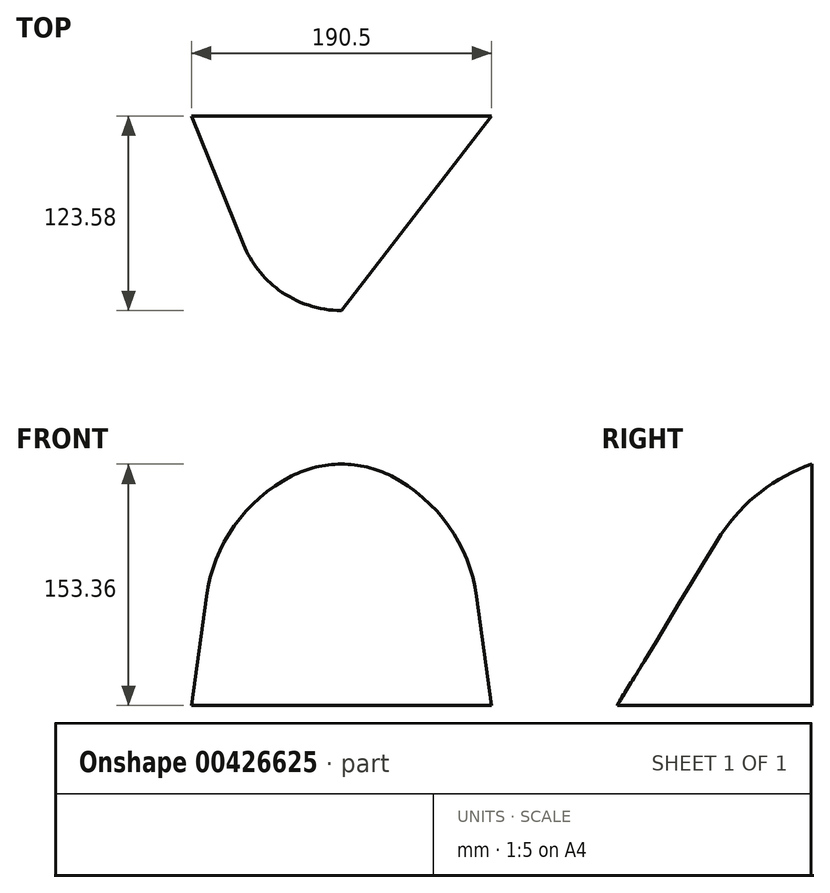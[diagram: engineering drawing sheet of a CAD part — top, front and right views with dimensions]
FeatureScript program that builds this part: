
annotation { "Feature Type Name" : "Feature", "Feature Type Description" : "" }
export const myFeature = defineFeature(function(context is Context, id is Id, definition is map)
    precondition{}
    {
        {
            var Q0;
            Q0=qCreatedBy(makeId("Front.planeOp"),FACE);
            var sketch = newSketch(context, id + "F0", { "sketchPlane" : qUnion([Q0])});
            skLineSegment(sketch, "E0", {"start": v(0, 111.3) * mm, "end": v(0, 0) * mm, "construction": true});
            skLineSegment(sketch, "E1", {"start": v(0, 0) * mm, "end": v(95.25, 0) * mm});
            skLineSegment(sketch, "E2", {"start": v(95.25, 0) * mm, "end": v(85.8, 69.13) * mm});
            skArc(sketch, "E3", {"start": v(85.8, 69.13) * mm, "mid": v(68.09, 114.03) * mm, "end": v(31.65, 145.7) * mm});
            skArc(sketch, "E4", {"start": v(31.65, 145.7) * mm, "mid": v(0, 153.36) * mm, "end": v(-31.65, 145.7) * mm});
            skArc(sketch, "E5.MirrorCS", {"start": v(-85.8, 69.13) * mm, "mid": v(-68.09, 114.03) * mm, "end": v(-31.65, 145.7) * mm});
            skLineSegment(sketch, "E6.MirrorCS", {"start": v(-95.25, 0) * mm, "end": v(-85.8, 69.13) * mm});
            skLineSegment(sketch, "E7.MirrorCS", {"start": v(0, 0) * mm, "end": v(-95.25, 0) * mm});
            skSolve(sketch);
        }
        {
            var Q0;
            Q0=qCreatedBy(makeId("Top.planeOp"),FACE);
            var sketch = newSketch(context, id + "F1", { "sketchPlane" : qUnion([Q0])});
            skLineSegment(sketch, "E8", {"start": v(-95.25, 0) * mm, "end": v(-62.12, -81.74) * mm, "construction": true});
            skArc(sketch, "E9", {"start": v(-62.12, -81.74) * mm, "mid": v(0, -123.58) * mm, "end": v(62.12, -81.74) * mm, "construction": true});
            skLineSegment(sketch, "E10", {"start": v(0, 0) * mm, "end": v(0, -123.58) * mm, "construction": true});
            skLineSegment(sketch, "E11", {"start": v(-95.25, 0) * mm, "end": v(95.25, 0) * mm, "construction": true});
            skLineSegment(sketch, "E12.MirrorCS", {"start": v(95.25, 0) * mm, "end": v(62.12, -81.74) * mm, "construction": true});
            skSolve(sketch);
        }
        {
            var Q0;
            Q0=qCreatedBy(makeId("Right.planeOp"),FACE);
            var sketch = newSketch(context, id + "F2", { "sketchPlane" : qUnion([Q0])});
            skArc(sketch, "E13", {"start": v(0, 153.36) * mm, "mid": v(-34.36, 134.32) * mm, "end": v(-60.2, 104.73) * mm, "construction": true});
            skLineSegment(sketch, "E14", {"start": v(-60.2, 104.73) * mm, "end": v(-123.58, 0) * mm, "construction": true});
            skFitSpline(sketch, "E15", {"points": [v(0, 153.36) * mm, v(-123.58, 0) * mm], "startDerivative": vector(-133.46, -61.2) * mm, "endDerivative": vector(-210.33, -343.88) * mm});
            skSolve(sketch);
        }
        {
            var Q0;
            Q0=qCreatedBy(makeId("Right.planeOp"),FACE);
            var sketch = newSketch(context, id + "F3", { "sketchPlane" : qUnion([Q0])});
            skArc(sketch, "E16.0", {"start": v(0, 153.36) * mm, "mid": v(-34.36, 134.32) * mm, "end": v(-60.2, 104.73) * mm});
            skLineSegment(sketch, "E16.1", {"start": v(-60.2, 104.73) * mm, "end": v(-123.58, 0) * mm});
            skSolve(sketch);
        }
        {
            var Q0;
            Q0=qCreatedBy(makeId("Top.planeOp"),FACE);
            var sketch = newSketch(context, id + "F4", { "sketchPlane" : qUnion([Q0])});
            skLineSegment(sketch, "E17.0", {"start": v(-95.25, 0) * mm, "end": v(-62.12, -81.74) * mm});
            skArc(sketch, "E17.1", {"start": v(-62.12, -81.74) * mm, "mid": v(-52.97, -97.63) * mm, "end": v(-39.86, -110.44) * mm});
            skArc(sketch, "E18", {"start": v(-39.86, -110.44) * mm, "mid": v(-20.98, -120.21) * mm, "end": v(0, -123.58) * mm});
            skSolve(sketch);
        }
        {
            var Q0;
            Q0=makeQuery(id+"F0.imprint","IMPRINT",FACE,{"disambiguationData":[TD([[makeQuery(id+"F0.imprint","IMPRINT",EDGE,{"derivedFrom":sQuery(id+"F0.wireOp",EDGE,"E1")}),1.0]])]});
            var Q1;
            Q1=sQuery(id+"F2.wireOp",VERTEX,"E14.end");
            var Q2;
            Q2=makeQuery(id+"F0.imprint","IMPRINT",FACE,{"disambiguationData":[TD([[makeQuery(id+"F0.imprint","IMPRINT",EDGE,{"derivedFrom":sQuery(id+"F0.wireOp",EDGE,"E1")}),1.0]])]});
            var Q3;
            Q3=sQuery(id+"F1.wireOp",VERTEX,"E10.end");
            var Q4;
            Q4 = qConstructionFilter(qBodyType(qCreatedBy(id + "F3" ,EDGE), BodyType.WIRE), ConstructionObject.NO);
            var Q5;
            Q5 = qConstructionFilter(qBodyType(qCreatedBy(id + "F4" ,EDGE), BodyType.WIRE), ConstructionObject.NO);
            loft(context, id + "F5", {"bodyType" : ToolBodyType.SURFACE, "addGuides" : true, "sheetProfilesArray" : [{ "sheetProfileEntities" : qUnion([Q0]) }, { "sheetProfileEntities" : qUnion([Q1]) }], "wireProfilesArray" : [{ "wireProfileEntities" : qUnion([Q2]) }, { "wireProfileEntities" : qUnion([Q3]) }], "guidesArray" : [{ "guideEntities" : qUnion([Q4]), "guideDerivativeType" : LoftGuideDerivativeType.DEFAULT, "guideDerivativeMagnitude" : 1 }, { "guideEntities" : qUnion([Q5]), "guideDerivativeType" : LoftGuideDerivativeType.DEFAULT, "guideDerivativeMagnitude" : 1 }]});
        }
    });
